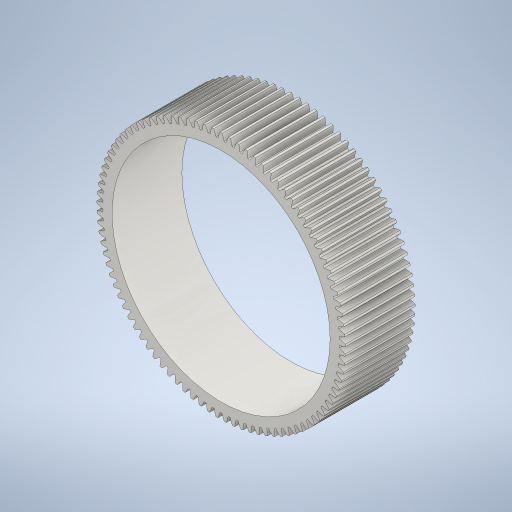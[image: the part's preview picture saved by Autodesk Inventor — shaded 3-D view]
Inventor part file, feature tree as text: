
AUTODESK INVENTOR PART (.ipt)
format: ipt  version: 2023.2 (Build 272271000, 271)  size: 692,224 bytes
history: native  units: mm (DEFAULTED — no unit token found)
features: plane x3, other x3, sketch x3, extrude x2
ambient origin geometry x8: Origin, YZ Plane, XZ Plane, XY Plane, X Axis, Y Axis, Z Axis, Center Point
bodies: Solid1 (feature_tree)
feature tree (11):
  extrude  "Extrusion1"  Depth=80.0mm TaperAngle=0.0deg
  plane  "Work Plane2"
  plane  "Work Plane8"
  plane  "Work Plane9"
  other  "Spur Gear"
  extrude  "Extrusion2"  Depth=10.0mm TaperAngle=0.0deg
  sketch  "Sketch1"  dims[d0=284.973278mm d1=80.0mm d2=0.0mm]
  sketch  "Sketch2"  dims[d3=279.0mm d4=10.0mm d5=0.0mm]
  other  "Srf1"
  sketch  "Sketch3"  dims[d16=280.0mm d17=0.0mm d34=0.337806mm d39=0.0mm d41=0.0mm d43=280.0mm d46=280.0mm d47=0.0mm d48=0.0mm d49=250.0mm d50=10.0mm d51=0.0mm]
  other  "Pitch Diameter"
